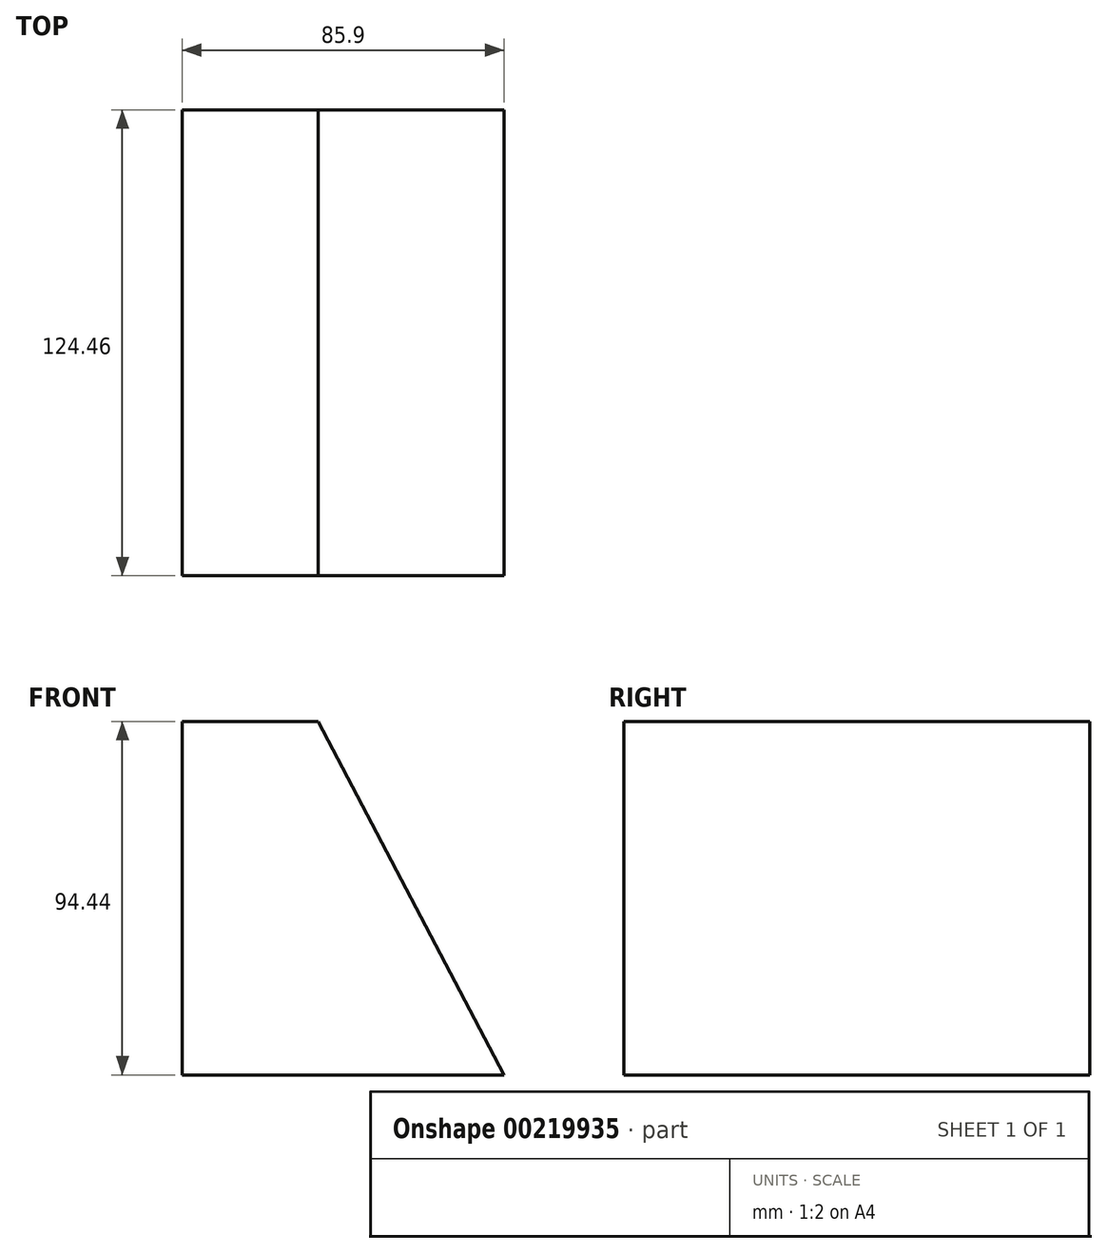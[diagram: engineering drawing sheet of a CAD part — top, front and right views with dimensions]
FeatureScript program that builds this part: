
annotation { "Feature Type Name" : "Feature", "Feature Type Description" : "" }
export const myFeature = defineFeature(function(context is Context, id is Id, definition is map)
    precondition{}
    {
        {
            var Q0;
            Q0=qCreatedBy(makeId("Front.planeOp"),FACE);
            var sketch = newSketch(context, id + "F0", { "sketchPlane" : qUnion([Q0])});
            skLineSegment(sketch, "E0.bottom", {"start": v(-36.25, 47.45) * mm, "end": v(49.65, 47.45) * mm});
            skLineSegment(sketch, "E0.top", {"start": v(-36.25, -47) * mm, "end": v(49.65, -47) * mm});
            skLineSegment(sketch, "E0.left", {"start": v(-36.25, 47.45) * mm, "end": v(-36.25, -47) * mm});
            skLineSegment(sketch, "E0.right", {"start": v(49.65, 47.45) * mm, "end": v(49.65, -47) * mm});
            skSolve(sketch);
        }
        {
            var Q0;
            Q0 = qSketchRegion(id + "F0", true);
            extrude(context, id + "F1", {"entities" : qUnion([Q0]), "depth" : 124.46 * mm});
        }
        {
            var Q0;
            Q0=makeQuery(id+"F1.opExtrude","CAP_FACE",FACE,{"disambiguationData":[OSD([sQuery(id+"F0.wireOp",EDGE,"E0.bottom"),sQuery(id+"F0.wireOp",EDGE,"E0.top"),sQuery(id+"F0.wireOp",EDGE,"E0.left"),sQuery(id+"F0.wireOp",EDGE,"E0.right")])],"isStart":false});
            var sketch = newSketch(context, id + "F2", { "sketchPlane" : qUnion([Q0])});
            skLineSegment(sketch, "E1", {"start": v(0, 47.45) * mm, "end": v(49.65, 47.45) * mm});
            skLineSegment(sketch, "E2", {"start": v(49.65, 47.45) * mm, "end": v(49.65, -47) * mm});
            skLineSegment(sketch, "E3", {"start": v(49.65, -47) * mm, "end": v(0, 47.45) * mm});
            skSolve(sketch);
        }
        {
            var Q0;
            Q0=makeQuery(id+"F2.imprint","IMPRINT",FACE,{"disambiguationData":[TD([[makeQuery(id+"F2.imprint","IMPRINT",EDGE,{"derivedFrom":sQuery(id+"F2.wireOp",EDGE,"E1")}),-1.0]])]});
            extrude(context, id + "F3", {"entities" : qUnion([Q0]), "operationType" : NewBodyOperationType.REMOVE, "endBound" : BoundingType.THROUGH_ALL, "oppositeDirection" : true, "depth" : 25.4 * mm});
        }
    });
